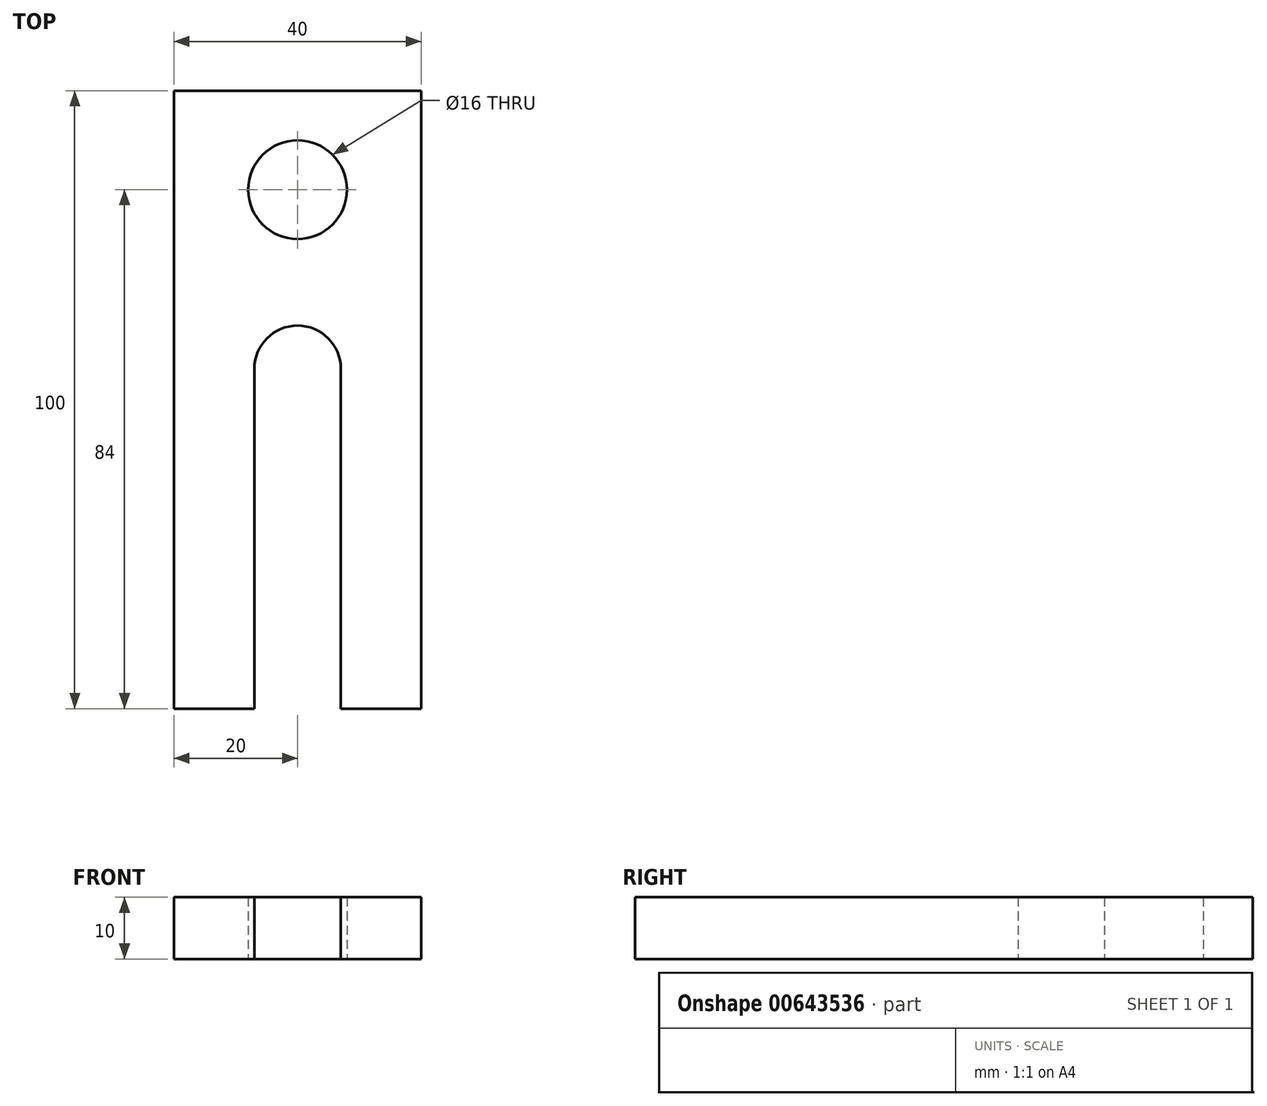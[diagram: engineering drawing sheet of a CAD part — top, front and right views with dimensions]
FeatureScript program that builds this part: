
annotation { "Feature Type Name" : "Feature", "Feature Type Description" : "" }
export const myFeature = defineFeature(function(context is Context, id is Id, definition is map)
    precondition{}
    {
        {
            var Q0;
            Q0=qCreatedBy(makeId("Top.planeOp"),FACE);
            var sketch = newSketch(context, id + "F0", { "sketchPlane" : qUnion([Q0])});
            skLineSegment(sketch, "E0.bottom", {"start": v(20, -50) * mm, "end": v(7, -50) * mm});
            skLineSegment(sketch, "E0.top", {"start": v(20, 50) * mm, "end": v(-20, 50) * mm});
            skLineSegment(sketch, "E0.left", {"start": v(20, -50) * mm, "end": v(20, 50) * mm});
            skLineSegment(sketch, "E0.right", {"start": v(-20, -50) * mm, "end": v(-20, 50) * mm});
            skPoint(sketch, "E0.middle", {"position": v(0, 0) * mm});
            skCircle(sketch, "E1", {"center": v(0, 34) * mm, "radius": 8 * mm});
            skArc(sketch, "E2", {"start": v(7, 5) * mm, "mid": v(0, 12) * mm, "end": v(-7, 5) * mm});
            skLineSegment(sketch, "E3", {"start": v(-7, 5) * mm, "end": v(-7, -50) * mm});
            skLineSegment(sketch, "E4", {"start": v(7, 5) * mm, "end": v(7, -50) * mm});
            skLineSegment(sketch, "E5.trimOffspring", {"start": v(-7, -50) * mm, "end": v(-20, -50) * mm});
            skSolve(sketch);
        }
        {
            var Q0;
            Q0 = qSketchRegion(id + "F0", true);
            extrude(context, id + "F1", {"entities" : qUnion([Q0]), "depth" : 10 * mm, "offsetDistance" : 25 * mm});
        }
    });
